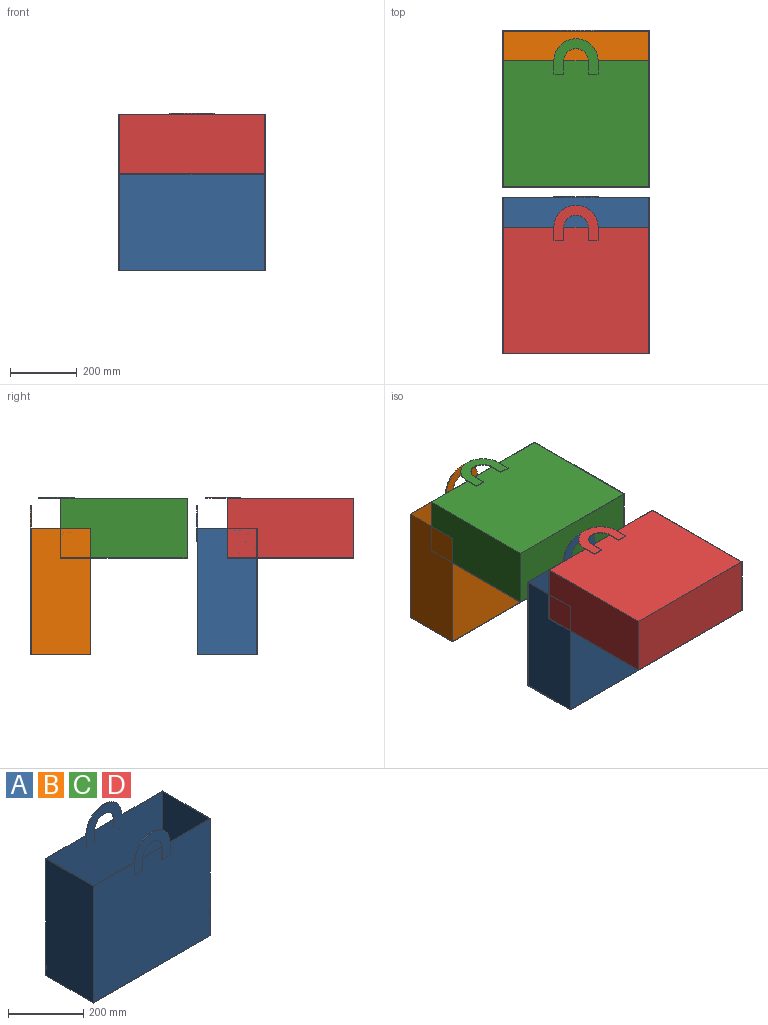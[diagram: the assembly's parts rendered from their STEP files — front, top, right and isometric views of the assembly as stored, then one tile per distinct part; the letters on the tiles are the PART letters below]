
ASSEMBLY  parts=4 mates=2
PART A: 32 faces, bbox 440x184x446.3 mm
  f0: cylinder r=66.32mm len=132.63mm, axis (0,1,0), area 625mm2, adj f2,f3,f12,f18,f19,f31
  f1: cylinder r=36.32mm len=72.63mm, axis (0,1,0), area 342.3mm2, adj f4,f12,f16,f21,f31
  f2: plane 180x153.68mm, normal (0,0,1), area 485.4mm2, adj f0,f6,f7,f9,f11,f12,f14,f25
  f3: plane 180x153.68mm, normal (0,0,1), area 485.4mm2, adj f0,f7,f8,f9,f12,f13,f14,f25
  f4: plane 72.63x1mm, normal (0,0,1), area 72.6mm2, adj f1,f7,f12
  f5: plane 72.63x1mm, normal (0,0,1), area 72.6mm2, adj f9,f14,f29
  f6: plane 380x180mm, normal (1,0,0), area 68400mm2, adj f2,f7,f9,f10
  f7: plane 440x380mm, normal (0,1,0), area 164800mm2, adj f2,f3,f4,f6,f8,f10,f16,f17
  f8: plane 380x180mm, normal (-1,0,0), area 68400mm2, adj f3,f7,f9,f10
  f9: plane 440x380mm, normal (0,-1,0), area 164800mm2, adj f2,f3,f5,f6,f8,f10,f22,f23
  f10: plane 440x180mm, normal (0,0,-1), area 79200mm2, adj f6,f7,f8,f9
  f11: plane 379x178mm, normal (-1,0,0), area 67462mm2, adj f2,f12,f14,f15
  f12: plane 445.32x438mm, normal (0,-1,0), area 170838.4mm2, adj f0,f1,f2,f3,f4,f11,f13,f15
  f13: plane 379x178mm, normal (1,0,0), area 67462mm2, adj f3,f12,f14,f15
  f14: plane 445.32x438mm, normal (0,1,0), area 170838.4mm2, adj f2,f3,f5,f11,f13,f15,f25,f29
  f15: plane 438x178mm, normal (0,0,1), area 77964mm2, adj f11,f12,f13,f14
  f16: plane 40x2mm, normal (-1,0,0), area 80mm2, adj f1,f7,f17,f31
  f17: plane 30x2mm, normal (0,0,-1), area 60mm2, adj f7,f16,f18,f31
  f18: plane 40x2mm, normal (1,0,0), area 80mm2, adj f0,f7,f17,f31
  f19: plane 40x2mm, normal (-1,0,0), area 80mm2, adj f0,f7,f20,f31
  f20: plane 30x2mm, normal (0,0,-1), area 60mm2, adj f7,f19,f21,f31
  f21: plane 40x2mm, normal (1,0,0), area 80mm2, adj f1,f7,f20,f31
  f22: plane 40x2mm, normal (-1,0,0), area 80mm2, adj f9,f23,f29,f30
  f23: plane 30x2mm, normal (0,0,-1), area 60mm2, adj f9,f22,f24,f30
  f24: plane 40x2mm, normal (1,0,0), area 80mm2, adj f9,f23,f25,f30
  f25: cylinder r=66.32mm len=132.63mm, axis (0,1,0), area 625mm2, adj f2,f3,f14,f24,f26,f30
  f26: plane 40x2mm, normal (-1,0,0), area 80mm2, adj f9,f25,f27,f30
  f27: plane 30x2mm, normal (0,0,-1), area 60mm2, adj f9,f26,f28,f30
  f28: plane 40x2mm, normal (1,0,0), area 80mm2, adj f9,f27,f29,f30
  f29: cylinder r=36.32mm len=72.63mm, axis (0,1,0), area 342.3mm2, adj f5,f14,f22,f28,f30
  f30: plane 132.63x106.32mm, normal (0,-1,0), area 7236.4mm2, adj f22,f23,f24,f25,f26,f27,f28,f29
  f31: plane 132.63x106.32mm, normal (0,1,0), area 7236.4mm2, adj f0,f1,f16,f17,f18,f19,f20,f21
PART B: same geometry as A
PART C: same geometry as A
PART D: same geometry as A
PLACE A t=(0,44.71,-315.42)mm
PLACE B t=(0,544.71,-315.42)mm
PLACE C rot(axis=(-1,0,0),90deg) t=(0,164.71,64.58)mm
PLACE D rot(axis=(-1,0,0),90deg) t=(0,-335.29,64.58)mm
MATE revolute B.f6 <-> C.f6  axis (1,0,0) through (220,544.71,64.58)mm
MATE planar C.f6 <-> B.f6  axis (1,0,0) through (220,354.71,64.58)mm
